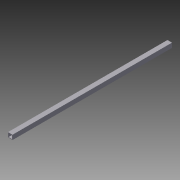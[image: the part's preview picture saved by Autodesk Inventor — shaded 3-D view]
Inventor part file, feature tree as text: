
AUTODESK INVENTOR PART (.ipt)
format: ipt  version: 2012 (Build 160160000, 160)  size: 78,848 bytes
history: native  units: in
note: dims shown in document units (in); Inventor stores cm internally (conversion verified against a paired STEP export)
features: extrude x1, other x1, shell x1, sketch x1
ambient origin geometry x8: Origin, YZ Plane, XZ Plane, XY Plane, X Axis, Y Axis, Z Axis, Center Point
bodies: Solid1 (feature_tree)
feature tree (4):
  extrude  "Extrusion1"  Depth=1.0in
  other  "Alias Freeform1"
  shell  "Shell1"  Thickness=25.0in
  sketch  "Sketch1"  dims[d0=1.0in d1=1.0in d2=25.0in d3=0.0in d4=0.125in]
